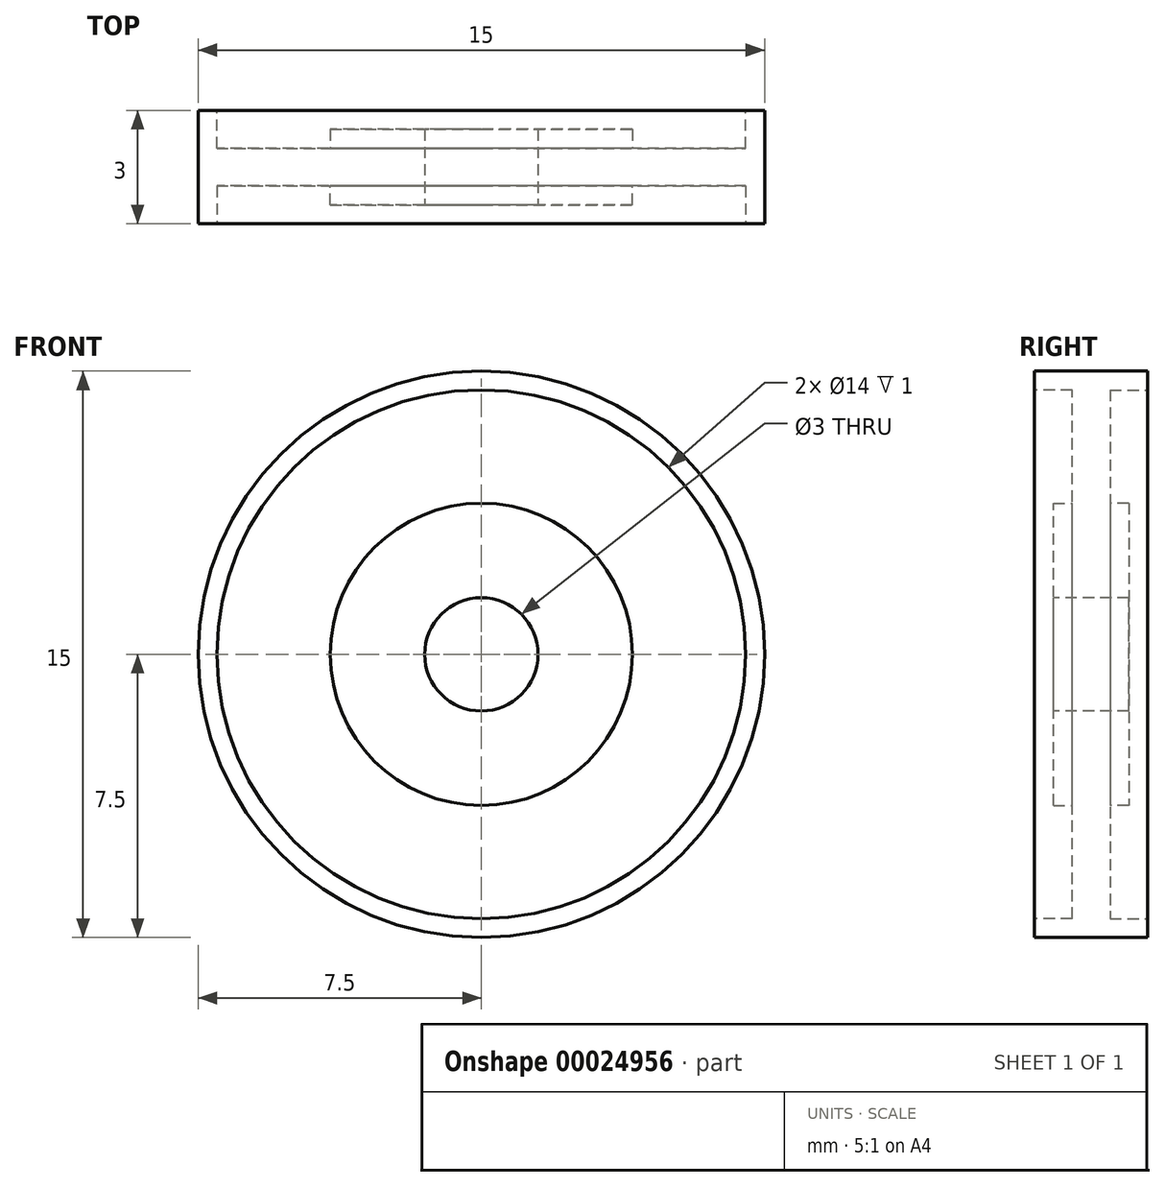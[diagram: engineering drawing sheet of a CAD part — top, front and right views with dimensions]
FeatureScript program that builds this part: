
annotation { "Feature Type Name" : "Feature", "Feature Type Description" : "" }
export const myFeature = defineFeature(function(context is Context, id is Id, definition is map)
    precondition{}
    {
        {
            var Q0;
            Q0=qCreatedBy(makeId("Front.planeOp"),FACE);
            var sketch = newSketch(context, id + "F0", { "sketchPlane" : qUnion([Q0])});
            skLineSegment(sketch, "E0", {"start": v(0, 0) * mm, "end": v(0, 7.5) * mm});
            skCircle(sketch, "E1", {"center": v(0, 0) * mm, "radius": 7.5 * mm});
            skSolve(sketch);
        }
        {
            var Q0;
            Q0=makeQuery(id+"F0.imprint","IMPRINT",FACE,{"disambiguationData":[TD([[makeQuery(id+"F0.imprint","IMPRINT",EDGE,{"derivedFrom":sQuery(id+"F0.wireOp",EDGE,"E1")}),1.0]])]});
            extrude(context, id + "F1", {"entities" : qUnion([Q0]), "endBound" : BoundingType.SYMMETRIC, "depth" : 3 * mm});
        }
        {
            var Q0;
            Q0=makeQuery(id+"F1.opExtrude","CAP_FACE",FACE,{"disambiguationData":[OSD([sQuery(id+"F0.wireOp",EDGE,"E1")])],"isStart":false});
            var sketch = newSketch(context, id + "F2", { "sketchPlane" : qUnion([Q0])});
            skLineSegment(sketch, "E2", {"start": v(0, 0) * mm, "end": v(0, 7.5) * mm});
            skLineSegment(sketch, "E3", {"start": v(0, 0) * mm, "end": v(7.5, 0) * mm});
            skLineSegment(sketch, "E4", {"start": v(0, 0) * mm, "end": v(0, -7.5) * mm});
            skLineSegment(sketch, "E5", {"start": v(0, 0) * mm, "end": v(-7.5, 0) * mm});
            skCircle(sketch, "E6", {"center": v(0, 0) * mm, "radius": 7 * mm});
            skCircle(sketch, "E7", {"center": v(0, 0) * mm, "radius": 4 * mm});
            skLineSegment(sketch, "E8", {"start": v(0, 0) * mm, "end": v(-4.95, 4.95) * mm});
            skLineSegment(sketch, "E9", {"start": v(0, 0) * mm, "end": v(-4.95, -4.95) * mm});
            skLineSegment(sketch, "E10", {"start": v(0, 0) * mm, "end": v(4.95, -4.95) * mm});
            skLineSegment(sketch, "E11", {"start": v(0, 0) * mm, "end": v(4.95, 4.95) * mm});
            skCircle(sketch, "E12", {"center": v(0, 0) * mm, "radius": 1.5 * mm});
            skPoint(sketch, "E13", {"position": v(-2.83, 2.83) * mm});
            skPoint(sketch, "E14", {"position": v(-2.83, -2.83) * mm});
            skPoint(sketch, "E15", {"position": v(2.83, -2.83) * mm});
            skPoint(sketch, "E16", {"position": v(2.83, 2.83) * mm});
            skPoint(sketch, "E17", {"position": v(-3.89, 3.89) * mm});
            skPoint(sketch, "E18", {"position": v(-3.89, -3.89) * mm});
            skPoint(sketch, "E19", {"position": v(3.89, -3.89) * mm});
            skPoint(sketch, "E20", {"position": v(3.89, 3.89) * mm});
            skLineSegment(sketch, "E21", {"start": v(-4.95, 4.95) * mm, "end": v(-2.83, 2.83) * mm});
            skLineSegment(sketch, "E22", {"start": v(4.95, 4.95) * mm, "end": v(2.83, 2.83) * mm});
            skLineSegment(sketch, "E23", {"start": v(-2.83, -2.83) * mm, "end": v(-4.95, -4.95) * mm});
            skLineSegment(sketch, "E24", {"start": v(2.83, -2.83) * mm, "end": v(4.95, -4.95) * mm});
            skCircle(sketch, "E25", {"center": v(-3.89, 3.89) * mm, "radius": 1.5 * mm});
            skCircle(sketch, "E26", {"center": v(3.89, 3.89) * mm, "radius": 1.5 * mm});
            skCircle(sketch, "E27", {"center": v(3.89, -3.89) * mm, "radius": 1.5 * mm});
            skCircle(sketch, "E28", {"center": v(-3.89, -3.89) * mm, "radius": 1.5 * mm});
            skSolve(sketch);
        }
        {
            var Q0;
            {var subQ1=sQuery(id+"F2.wireOp",EDGE,"E21");Q0=makeQuery(id+"F2.imprint","IMPRINT",FACE,{"disambiguationData":[TD([[makeQuery(id+"F2.imprint","IMPRINT",EDGE,{"derivedFrom":subQ1}),1.0]])]});}
            var Q1;
            {var subQ1=sQuery(id+"F2.wireOp",EDGE,"E21");Q1=makeQuery(id+"F2.imprint","IMPRINT",FACE,{"disambiguationData":[TD([[makeQuery(id+"F2.imprint","IMPRINT",EDGE,{"derivedFrom":subQ1}),-1.0]])]});}
            var Q2;
            {var subQ1=sQuery(id+"F2.wireOp",EDGE,"E22");Q2=makeQuery(id+"F2.imprint","IMPRINT",FACE,{"disambiguationData":[TD([[makeQuery(id+"F2.imprint","IMPRINT",EDGE,{"derivedFrom":subQ1}),-1.0]])]});}
            var Q3;
            {var subQ1=sQuery(id+"F2.wireOp",EDGE,"E22");Q3=makeQuery(id+"F2.imprint","IMPRINT",FACE,{"disambiguationData":[TD([[makeQuery(id+"F2.imprint","IMPRINT",EDGE,{"derivedFrom":subQ1}),1.0]])]});}
            var Q4;
            {var subQ0=sQuery(id+"F2.wireOp",EDGE,"E12");var subQ3=sQuery(id+"F2.wireOp",EDGE,"E3");var subQ4=makeQuery(id+"F2.imprint","INTERSECT",VERTEX,{"derivedFrom":[subQ3,subQ0]});Q4=makeQuery(id+"F2.imprint","IMPRINT",FACE,{"disambiguationData":[TD([[makeQuery(id+"F2.imprint","IMPRINT",EDGE,{"disambiguationData":[TD([[subQ4,-1.0]])],"derivedFrom":subQ0}),1.0]])]});}
            var Q5;
            {var subQ0=sQuery(id+"F2.wireOp",EDGE,"E12");var subQ3=sQuery(id+"F2.wireOp",EDGE,"E2");var subQ4=makeQuery(id+"F2.imprint","INTERSECT",VERTEX,{"derivedFrom":[subQ3,subQ0]});Q5=makeQuery(id+"F2.imprint","IMPRINT",FACE,{"disambiguationData":[TD([[makeQuery(id+"F2.imprint","IMPRINT",EDGE,{"disambiguationData":[TD([[subQ4,1.0]])],"derivedFrom":subQ0}),1.0]])]});}
            var Q6;
            {var subQ0=sQuery(id+"F2.wireOp",EDGE,"E12");var subQ3=sQuery(id+"F2.wireOp",EDGE,"E2");var subQ4=makeQuery(id+"F2.imprint","INTERSECT",VERTEX,{"derivedFrom":[subQ3,subQ0]});Q6=makeQuery(id+"F2.imprint","IMPRINT",FACE,{"disambiguationData":[TD([[makeQuery(id+"F2.imprint","IMPRINT",EDGE,{"disambiguationData":[TD([[subQ4,-1.0]])],"derivedFrom":subQ0}),1.0]])]});}
            var Q7;
            {var subQ0=sQuery(id+"F2.wireOp",EDGE,"E12");var subQ3=sQuery(id+"F2.wireOp",EDGE,"E5");var subQ4=makeQuery(id+"F2.imprint","INTERSECT",VERTEX,{"derivedFrom":[subQ3,subQ0]});Q7=makeQuery(id+"F2.imprint","IMPRINT",FACE,{"disambiguationData":[TD([[makeQuery(id+"F2.imprint","IMPRINT",EDGE,{"disambiguationData":[TD([[subQ4,1.0]])],"derivedFrom":subQ0}),1.0]])]});}
            var Q8;
            {var subQ0=sQuery(id+"F2.wireOp",EDGE,"E12");var subQ3=sQuery(id+"F2.wireOp",EDGE,"E5");var subQ4=makeQuery(id+"F2.imprint","INTERSECT",VERTEX,{"derivedFrom":[subQ3,subQ0]});Q8=makeQuery(id+"F2.imprint","IMPRINT",FACE,{"disambiguationData":[TD([[makeQuery(id+"F2.imprint","IMPRINT",EDGE,{"disambiguationData":[TD([[subQ4,-1.0]])],"derivedFrom":subQ0}),1.0]])]});}
            var Q9;
            {var subQ0=sQuery(id+"F2.wireOp",EDGE,"E12");var subQ3=sQuery(id+"F2.wireOp",EDGE,"E4");var subQ4=makeQuery(id+"F2.imprint","INTERSECT",VERTEX,{"derivedFrom":[subQ3,subQ0]});Q9=makeQuery(id+"F2.imprint","IMPRINT",FACE,{"disambiguationData":[TD([[makeQuery(id+"F2.imprint","IMPRINT",EDGE,{"disambiguationData":[TD([[subQ4,1.0]])],"derivedFrom":subQ0}),1.0]])]});}
            var Q10;
            {var subQ0=sQuery(id+"F2.wireOp",EDGE,"E12");var subQ3=sQuery(id+"F2.wireOp",EDGE,"E4");var subQ4=makeQuery(id+"F2.imprint","INTERSECT",VERTEX,{"derivedFrom":[subQ3,subQ0]});Q10=makeQuery(id+"F2.imprint","IMPRINT",FACE,{"disambiguationData":[TD([[makeQuery(id+"F2.imprint","IMPRINT",EDGE,{"disambiguationData":[TD([[subQ4,-1.0]])],"derivedFrom":subQ0}),1.0]])]});}
            var Q11;
            {var subQ0=sQuery(id+"F2.wireOp",EDGE,"E12");var subQ3=sQuery(id+"F2.wireOp",EDGE,"E3");var subQ4=makeQuery(id+"F2.imprint","INTERSECT",VERTEX,{"derivedFrom":[subQ3,subQ0]});Q11=makeQuery(id+"F2.imprint","IMPRINT",FACE,{"disambiguationData":[TD([[makeQuery(id+"F2.imprint","IMPRINT",EDGE,{"disambiguationData":[TD([[subQ4,1.0]])],"derivedFrom":subQ0}),1.0]])]});}
            var Q12;
            {var subQ1=sQuery(id+"F2.wireOp",EDGE,"E24");Q12=makeQuery(id+"F2.imprint","IMPRINT",FACE,{"disambiguationData":[TD([[makeQuery(id+"F2.imprint","IMPRINT",EDGE,{"derivedFrom":subQ1}),1.0]])]});}
            var Q13;
            {var subQ1=sQuery(id+"F2.wireOp",EDGE,"E24");Q13=makeQuery(id+"F2.imprint","IMPRINT",FACE,{"disambiguationData":[TD([[makeQuery(id+"F2.imprint","IMPRINT",EDGE,{"derivedFrom":subQ1}),-1.0]])]});}
            var Q14;
            {var subQ1=sQuery(id+"F2.wireOp",EDGE,"E23");Q14=makeQuery(id+"F2.imprint","IMPRINT",FACE,{"disambiguationData":[TD([[makeQuery(id+"F2.imprint","IMPRINT",EDGE,{"derivedFrom":subQ1}),1.0]])]});}
            var Q15;
            {var subQ1=sQuery(id+"F2.wireOp",EDGE,"E23");Q15=makeQuery(id+"F2.imprint","IMPRINT",FACE,{"disambiguationData":[TD([[makeQuery(id+"F2.imprint","IMPRINT",EDGE,{"derivedFrom":subQ1}),-1.0]])]});}
            extrude(context, id + "F3", {"entities" : qUnion([Q0, Q1, Q2, Q3, Q4, Q5, Q6, Q7, Q8, Q9, Q10, Q11, Q12, Q13, Q14, Q15]), "operationType" : NewBodyOperationType.REMOVE, "oppositeDirection" : true, "depth" : 25 * mm});
        }
        {
            var Q0;
            Q0=makeQuery(id+"F1.opExtrude","CAP_FACE",FACE,{"disambiguationData":[OSD([sQuery(id+"F0.wireOp",EDGE,"E1")])],"isStart":false});
            var sketch = newSketch(context, id + "F4", { "sketchPlane" : qUnion([Q0])});
            skCircle(sketch, "E29", {"center": v(0, 0) * mm, "radius": 7 * mm});
            skSolve(sketch);
        }
        {
            var Q0;
            Q0 = qSketchRegion(id + "F4", true);
            extrude(context, id + "F5", {"entities" : qUnion([Q0]), "operationType" : NewBodyOperationType.REMOVE, "oppositeDirection" : true, "depth" : 1 * mm});
        }
        {
            var Q0;
            Q0=makeQuery(id+"F1.opExtrude","CAP_FACE",FACE,{"disambiguationData":[OSD([sQuery(id+"F0.wireOp",EDGE,"E1")])],"isStart":true});
            var sketch = newSketch(context, id + "F6", { "sketchPlane" : qUnion([Q0])});
            skCircle(sketch, "E30", {"center": v(0, 0) * mm, "radius": 7 * mm});
            skSolve(sketch);
        }
        {
            var Q0;
            Q0 = qSketchRegion(id + "F6", true);
            extrude(context, id + "F7", {"entities" : qUnion([Q0]), "operationType" : NewBodyOperationType.REMOVE, "oppositeDirection" : true, "depth" : 1 * mm});
        }
        {
            var Q0;
            Q0=makeQuery(id+"F7.boolean.opBoolean","COPY",FACE,{"derivedFrom":makeQuery(id+"F7.opExtrude","CAP_FACE",FACE,{"disambiguationData":[OSD([sQuery(id+"F6.wireOp",EDGE,"E30")])],"isStart":false})});
            var sketch = newSketch(context, id + "F8", { "sketchPlane" : qUnion([Q0])});
            skCircle(sketch, "E31", {"center": v(0, 0) * mm, "radius": 4 * mm});
            skCircle(sketch, "E32", {"center": v(0, 0) * mm, "radius": 1.5 * mm});
            skSolve(sketch);
        }
        {
            var Q0;
            Q0 = qSketchRegion(id + "F8", true);
            extrude(context, id + "F9", {"entities" : qUnion([Q0]), "operationType" : NewBodyOperationType.ADD, "endBound" : BoundingType.SYMMETRIC, "depth" : 1 * mm});
        }
        {
            var Q0;
            Q0=makeQuery(id+"F5.boolean.opBoolean","COPY",FACE,{"derivedFrom":makeQuery(id+"F5.opExtrude","CAP_FACE",FACE,{"disambiguationData":[OSD([sQuery(id+"F4.wireOp",EDGE,"E29")])],"isStart":false})});
            var sketch = newSketch(context, id + "F10", { "sketchPlane" : qUnion([Q0])});
            skCircle(sketch, "E33", {"center": v(0, 0) * mm, "radius": 4 * mm});
            skCircle(sketch, "E34", {"center": v(0, 0) * mm, "radius": 1.5 * mm});
            skSolve(sketch);
        }
        {
            var Q0;
            Q0 = qSketchRegion(id + "F10", true);
            extrude(context, id + "F11", {"entities" : qUnion([Q0]), "operationType" : NewBodyOperationType.ADD, "depth" : 0.5 * mm});
        }
    });
